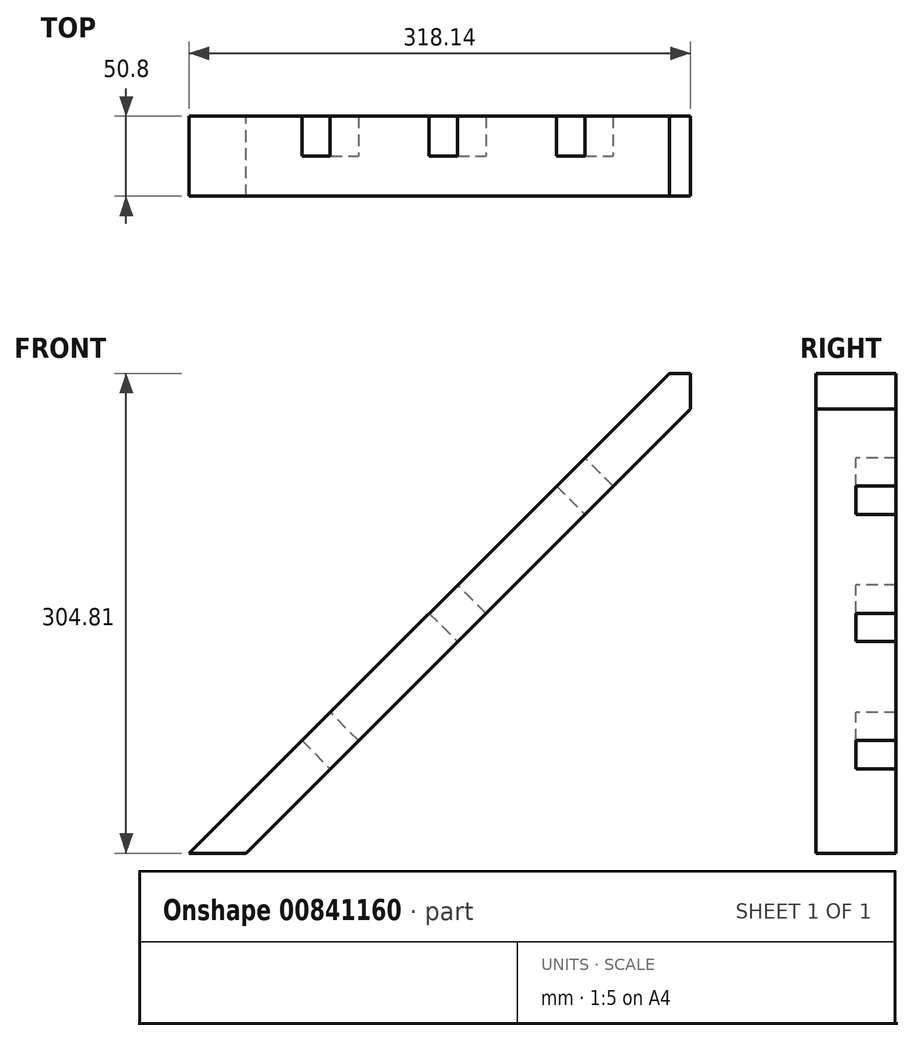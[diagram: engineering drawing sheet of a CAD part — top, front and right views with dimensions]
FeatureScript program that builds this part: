
annotation { "Feature Type Name" : "Feature", "Feature Type Description" : "" }
export const myFeature = defineFeature(function(context is Context, id is Id, definition is map)
    precondition{}
    {
        {
            var Q0;
            Q0=qCreatedBy(makeId("Front.planeOp"),FACE);
            var sketch = newSketch(context, id + "F0", { "sketchPlane" : qUnion([Q0])});
            skLineSegment(sketch, "E0", {"start": v(0, 0) * mm, "end": v(304.8, 304.8) * mm});
            skLineSegment(sketch, "E1", {"start": v(0, 0) * mm, "end": v(35.92, 0) * mm});
            skLineSegment(sketch, "E2", {"start": v(35.92, 0) * mm, "end": v(318.14, 282.22) * mm});
            skLineSegment(sketch, "E3", {"start": v(304.8, 304.8) * mm, "end": v(318.14, 304.8) * mm});
            skLineSegment(sketch, "E4", {"start": v(318.14, 282.22) * mm, "end": v(318.14, 304.8) * mm});
            skSolve(sketch);
        }
        {
            var Q0;
            Q0=makeQuery(id+"F0.imprint","IMPRINT",FACE,{"disambiguationData":[TD([[makeQuery(id+"F0.imprint","IMPRINT",EDGE,{"derivedFrom":sQuery(id+"F0.wireOp",EDGE,"E0")}),-1.0]])]});
            extrude(context, id + "F1", {"entities" : qUnion([Q0]), "depth" : 50.8 * mm, "offsetDistance" : 25.4 * mm});
        }
        {
            var Q0;
            Q0=qCreatedBy(makeId("Front.planeOp"),FACE);
            var sketch = newSketch(context, id + "F2", { "sketchPlane" : qUnion([Q0])});
            skLineSegment(sketch, "E5", {"start": v(59.64, 83.5) * mm, "end": v(106.89, 36.26) * mm});
            skLineSegment(sketch, "E6", {"start": v(106.89, 36.26) * mm, "end": v(124.85, 54.22) * mm});
            skLineSegment(sketch, "E7", {"start": v(124.85, 54.22) * mm, "end": v(77.6, 101.46) * mm});
            skLineSegment(sketch, "E8", {"start": v(77.6, 101.46) * mm, "end": v(59.64, 83.5) * mm});
            skLineSegment(sketch, "E9", {"start": v(217.18, 249.26) * mm, "end": v(266.15, 200.29) * mm});
            skLineSegment(sketch, "E10", {"start": v(266.15, 200.29) * mm, "end": v(284.1, 218.25) * mm});
            skLineSegment(sketch, "E11", {"start": v(284.1, 218.25) * mm, "end": v(235.14, 267.22) * mm});
            skLineSegment(sketch, "E12", {"start": v(235.14, 267.22) * mm, "end": v(217.18, 249.26) * mm});
            skLineSegment(sketch, "E13", {"start": v(133.7, 171.08) * mm, "end": v(190.51, 114.28) * mm});
            skLineSegment(sketch, "E14", {"start": v(190.51, 114.28) * mm, "end": v(208.47, 132.24) * mm});
            skLineSegment(sketch, "E15", {"start": v(208.47, 132.24) * mm, "end": v(151.67, 189.04) * mm});
            skLineSegment(sketch, "E16", {"start": v(151.67, 189.04) * mm, "end": v(133.7, 171.08) * mm});
            skSolve(sketch);
        }
        {
            var Q0;
            Q0=makeQuery(id+"F2.imprint","IMPRINT",FACE,{"disambiguationData":[TD([[makeQuery(id+"F2.imprint","IMPRINT",EDGE,{"derivedFrom":sQuery(id+"F2.wireOp",EDGE,"E9")}),1.0]])]});
            var Q1;
            Q1=makeQuery(id+"F2.imprint","IMPRINT",FACE,{"disambiguationData":[TD([[makeQuery(id+"F2.imprint","IMPRINT",EDGE,{"derivedFrom":sQuery(id+"F2.wireOp",EDGE,"E5")}),1.0]])]});
            var Q2;
            Q2=makeQuery(id+"F2.imprint","IMPRINT",FACE,{"disambiguationData":[TD([[makeQuery(id+"F2.imprint","IMPRINT",EDGE,{"derivedFrom":sQuery(id+"F2.wireOp",EDGE,"E13")}),1.0]])]});
            extrude(context, id + "F3", {"entities" : qUnion([Q0, Q1, Q2]), "operationType" : NewBodyOperationType.REMOVE, "depth" : 25.4 * mm, "offsetDistance" : 25.4 * mm});
        }
    });
